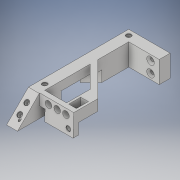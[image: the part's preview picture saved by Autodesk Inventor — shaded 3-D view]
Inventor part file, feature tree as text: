
AUTODESK INVENTOR PART (.ipt)
format: ipt  version: 2019 (Build 230136000, 136)  size: 416,256 bytes
history: native  units: in
note: dims shown in document units (in); Inventor stores cm internally (conversion verified against a paired STEP export)
features: sketch x21, extrude x14, hole x8, chamfer x1
ambient origin geometry x8: Origin, YZ Plane, XZ Plane, XY Plane, X Axis, Y Axis, Z Axis, Center Point
bodies: Solid1 (feature_tree)
feature tree (44):
  extrude  "Extrusion1"  Depth=1.1024in TaperAngle=0.0deg
  extrude  "Extrusion4"  Depth=0.1181in
  hole  "Hole2"  [1 undecoded]
  hole  "Hole3"  [1 undecoded]
  hole  "Hole4"  [1 undecoded]
  hole  "Hole5"  [1 undecoded]
  sketch  "Sketch6"  dims[d19=4.4488in d22=0.1181in]
  hole  "Hole6"  [1 undecoded]
  extrude  "Extrusion5"  Depth=0.1969in
  sketch  "Sketch16"  dims[d51=0.1969in]
  hole  "Hole11"  [1 undecoded]
  extrude  "Extrusion22"  Depth=0.1969in
  extrude  "Extrusion23"  Depth=0.1969in
  chamfer  "Chamfer3"  Distance=0.5118in
  extrude  "Extrusion24"  Depth=0.1969in
  extrude  "Extrusion25"  Depth=1.378in TaperAngle=0.0deg
  extrude  "Extrusion26"  Depth=0.1181in
  extrude  "Extrusion27"  Depth=0.1181in
  hole  "Hole12"  [1 undecoded]
  hole  "Hole13"  [1 undecoded]
  extrude  "Extrusion28"  Depth=1.3386in
  extrude  "Extrusion29"  Depth=0.7874in
  extrude  "Extrusion30"  Depth=0.315in TaperAngle=0.0deg
  extrude  "Extrusion31"  Depth=0.7874in
  extrude  "Extrusion32"  TaperAngle=45.0deg  [1 undecoded]
  sketch  "Sketch4"  dims[d4=0.3937in d5=0.0in d15=1.1024in d16=0.0in]
  sketch  "Sketch7"  dims[d23=0.1181in d25=0.0787in]
  sketch  "Sketch8"  dims[d26=0.7874in d27=0.3937in]
  sketch  "Sketch9"  dims[d39=0.1181in d40=0.1969in]
  sketch  "Sketch10"  dims[d41=0.079in d42=0.197in d43=0.1575in d44=0.0394in d45=0.5635in d46=0.299in d47=0.0in d48=0.1969in]
  sketch  "Sketch12"  dims[d49=1.1811in d50=0.1969in]
  sketch  "Sketch35"  dims[d54=0.163in d55=0.3937in d56=0.1575in d57=0.0394in d58=0.5635in d59=0.3937in d60=0.0in d61=0.1969in]
  sketch  "Sketch36"  dims[d62=0.1969in d63=0.3937in]
  sketch  "Sketch37"  dims[d64=0.3937in d65=0.1969in]
  sketch  "Sketch38"  dims[d66=0.1575in d67=0.3937in d68=0.1772in d69=0.0236in d70=0.5635in d71=0.1575in d72=0.0in d73=0.1969in]
  sketch  "Sketch39"  dims[d74=0.3937in]
  sketch  "Sketch40"  dims[d75=0.1969in]
  sketch  "Sketch41"  dims[d76=0.1969in]
  sketch  "Sketch42"  dims[d77=0.1575in d78=0.3937in d79=0.1772in d80=0.0236in d81=0.5635in d82=0.1575in d83=0.0in]
  sketch  "Sketch43"  dims[d84=0.315in]
  sketch  "Sketch44"  dims[d85=0.1969in]
  sketch  "Sketch45"  dims[d86=0.315in]
  sketch  "Sketch46"  dims[d87=0.1969in]
  sketch  "Sketch47"  dims[d88=0.1339in d89=0.3937in d90=0.2717in d91=0.25in d92=0.6181in d93=0.3937in d94=0.8108in d97=0.5118in d98=0.1969in d106=1.378in d107=0.0in d124=0.1181in d125=0.1181in d240=0.1575in d241=0.2362in d242=0.1772in d243=0.0236in d244=90.0deg d245=0.1575in d246=0.0in d247=0.1969in d248=1.3386in d249=0.0in d250=1.3386in d251=0.7874in d252=0.1378in d253=0.0in d254=0.7874in d255=0.0787in d256=0.0118in d258=45.0deg d259=0.0787in d260=0.9055in d261=0.2756in d262=0.1378in d263=0.1181in d264=0.4724in d265=0.0in d266=1.2205in d267=0.1969in d268=0.7874in d269=0.0in d270=0.1181in d271=0.3937in d272=0.1969in d273=0.7874in d274=0.0in d275=0.3937in d276=0.1969in d277=0.7874in d278=0.0in d279=0.1772in d280=0.2067in d281=0.1575in d282=0.2362in d283=0.1772in d284=0.0236in d285=90.0deg d286=0.1575in d287=0.0in d288=0.1772in d289=0.2067in d290=0.1339in d291=0.2362in d292=0.2717in d293=0.0236in d294=0.6181in d295=0.1575in d296=0.0in d297=0.5118in d298=0.4331in d299=0.3937in d300=0.0in d301=0.0787in d302=0.2756in d303=0.4331in d304=0.3937in d305=0.0in d306=0.1575in d307=0.1181in d308=0.1575in d309=0.3937in d310=0.0in d311=0.1969in d312=0.3937in d313=0.315in d314=0.315in d315=0.315in d316=0.2362in d317=0.2362in d318=0.2362in d319=0.2362in d320=0.3937in d321=0.0in d322=0.1969in d323=0.315in d324=0.315in d325=0.315in d326=0.2362in d327=0.2362in d328=0.2362in d329=0.3937in d330=0.0in d95=0.3937in d96=0.8108in d99=0.315in]
note: 9 required parameter values undecoded (feature->parameter linkage not recoverable at this tier; creation-order binding heuristic only, values carry confidence <= 0.55)
